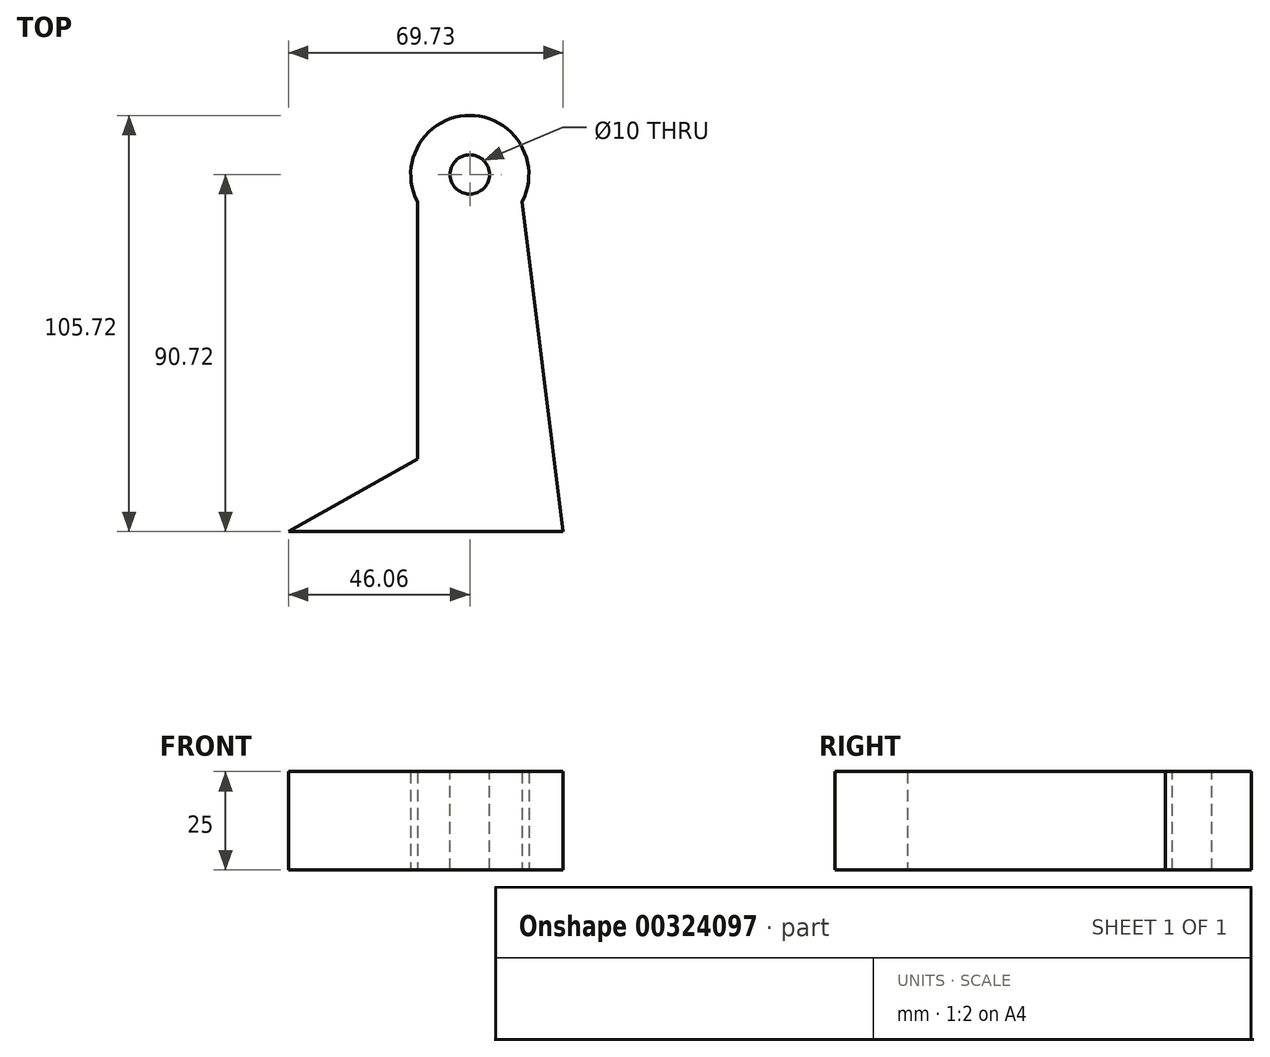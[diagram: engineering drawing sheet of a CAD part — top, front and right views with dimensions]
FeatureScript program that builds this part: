
annotation { "Feature Type Name" : "Feature", "Feature Type Description" : "" }
export const myFeature = defineFeature(function(context is Context, id is Id, definition is map)
    precondition{}
    {
        {
            var Q0;
            Q0=qCreatedBy(makeId("Top.planeOp"),FACE);
            var sketch = newSketch(context, id + "F0", { "sketchPlane" : qUnion([Q0])});
            skCircle(sketch, "E0", {"center": v(0, 0) * mm, "radius": 15 * mm});
            skLineSegment(sketch, "E1.bottom", {"start": v(13.33, -6.88) * mm, "end": v(-13.33, -6.88) * mm});
            skLineSegment(sketch, "E1.top", {"start": v(13.33, 6.88) * mm, "end": v(-13.33, 6.88) * mm});
            skLineSegment(sketch, "E1.left", {"start": v(13.33, -6.88) * mm, "end": v(13.33, 6.88) * mm});
            skLineSegment(sketch, "E1.right", {"start": v(-13.33, -6.88) * mm, "end": v(-13.33, 6.88) * mm});
            skLineSegment(sketch, "E2", {"start": v(-13.33, -6.88) * mm, "end": v(-13.33, -42.61) * mm});
            skLineSegment(sketch, "E3", {"start": v(-13.33, -42.61) * mm, "end": v(-13.33, -72.34) * mm});
            skLineSegment(sketch, "E4", {"start": v(-13.33, -72.34) * mm, "end": v(-46.06, -90.72) * mm});
            skLineSegment(sketch, "E5", {"start": v(-46.06, -90.72) * mm, "end": v(23.67, -90.72) * mm});
            skLineSegment(sketch, "E6", {"start": v(23.67, -90.72) * mm, "end": v(13.33, -6.88) * mm});
            skSolve(sketch);
        }
        {
            var Q0;
            Q0 = qSketchRegion(id + "F0", true);
            extrude(context, id + "F1", {"entities" : qUnion([Q0]), "depth" : 25 * mm});
        }
        {
            var Q0;
            Q0=makeQuery(id+"F1.opExtrude","CAP_FACE",FACE,{"disambiguationData":[OSD([sQuery(id+"F0.wireOp",EDGE,"E0"),sQuery(id+"F0.wireOp",EDGE,"E2"),sQuery(id+"F0.wireOp",EDGE,"E3"),sQuery(id+"F0.wireOp",EDGE,"E4"),sQuery(id+"F0.wireOp",EDGE,"E5"),sQuery(id+"F0.wireOp",EDGE,"E6")])],"isStart":false});
            var sketch = newSketch(context, id + "F2", { "sketchPlane" : qUnion([Q0])});
            skCircle(sketch, "E7", {"center": v(0, 0) * mm, "radius": 5 * mm});
            skSolve(sketch);
        }
        {
            var Q0;
            Q0 = qSketchRegion(id + "F2", true);
            extrude(context, id + "F3", {"entities" : qUnion([Q0]), "operationType" : NewBodyOperationType.REMOVE, "oppositeDirection" : true, "depth" : 25 * mm});
        }
    });
